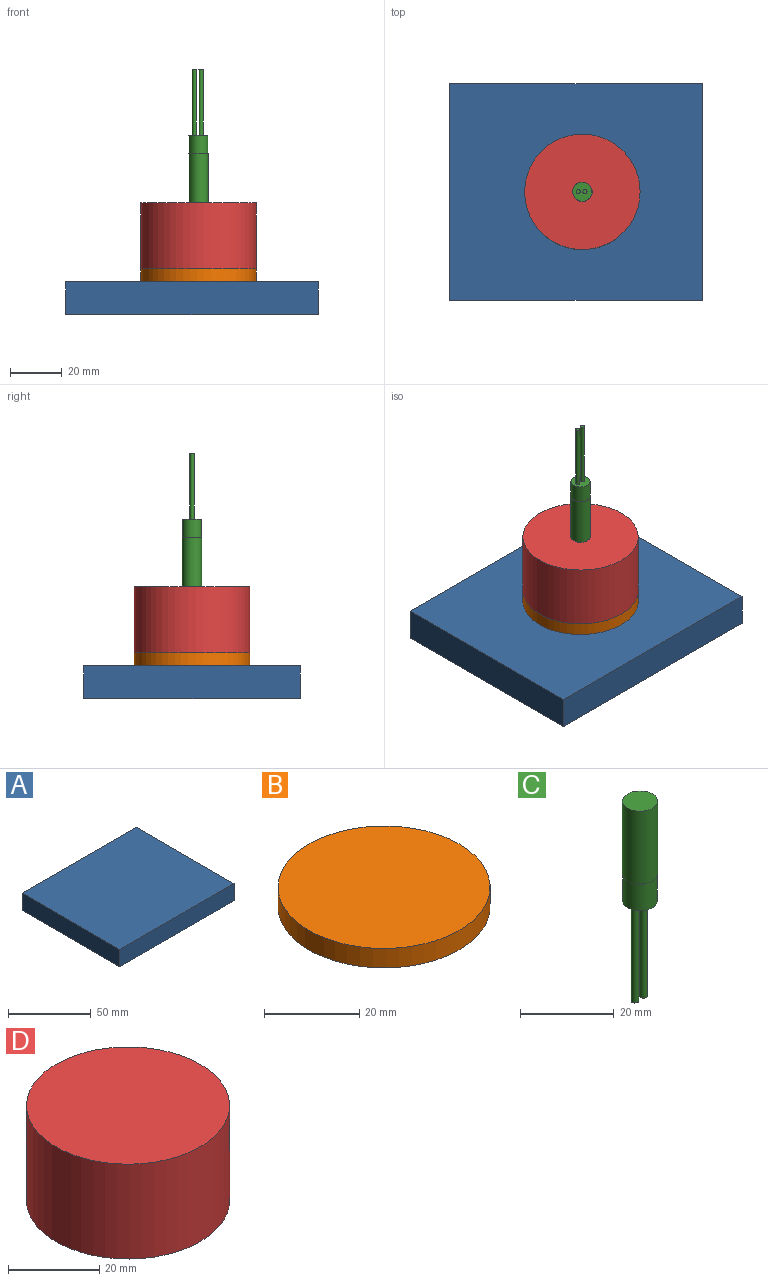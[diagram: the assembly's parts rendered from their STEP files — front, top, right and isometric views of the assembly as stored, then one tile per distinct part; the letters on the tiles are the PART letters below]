
ASSEMBLY  parts=4 mates=5
PART A: 6 faces, bbox 97.3x83.5x12.7 mm
  f0: plane 97.28x12.7mm, normal (0,1,0), area 1235.4mm2, adj f1,f3,f4,f5
  f1: plane 83.49x12.7mm, normal (-1,0,0), area 1060.3mm2, adj f0,f2,f4,f5
  f2: plane 97.28x12.7mm, normal (0,-1,0), area 1235.4mm2, adj f1,f3,f4,f5
  f3: plane 83.49x12.7mm, normal (1,0,0), area 1060.3mm2, adj f0,f2,f4,f5
  f4: plane 97.28x83.49mm, normal (0,0,1), area 8121.8mm2, adj f0,f1,f2,f3
  f5: plane 97.28x83.49mm, normal (0,0,-1), area 8121.8mm2, adj f0,f1,f2,f3
PART B: 3 faces, bbox 44.5x44.5x5 mm
  f0: cylinder r=22.23mm len=44.45mm, axis (0,0,-1), area 698.2mm2, adj f1,f2
  f1: plane 44.45x44.45mm, normal (0,0,1), area 1551.8mm2, adj f0
  f2: plane 44.45x44.45mm, normal (0,0,-1), area 1551.8mm2, adj f0
PART C: 9 faces, bbox 7.5x7.5x51.4 mm
  f0: cylinder r=3.68mm len=7.37mm, axis (0,0,1), area 161.6mm2, adj f1,f8
  f1: plane 7.37x7.37mm, normal (0,0,-1), area 38.7mm2, adj f0,f2,f4
  f2: cylinder r=0.79mm len=25.4mm, axis (0,0,1), area 125.7mm2, adj f1,f3
  f3: plane 1.57x1.57mm, normal (0,0,-1), area 1.9mm2, adj f2
  f4: cylinder r=0.79mm len=25.4mm, axis (0,0,1), area 125.7mm2, adj f1,f5
  f5: plane 1.57x1.57mm, normal (0,0,-1), area 1.9mm2, adj f4
  f6: cylinder r=3.75mm len=19.05mm, axis (0,0,-1), area 448.4mm2, adj f7,f8
  f7: plane 7.49x7.49mm, normal (0,0,1), area 44.1mm2, adj f6
  f8: plane 7.49x7.49mm, normal (0,0,-1), area 1.5mm2, adj f0,f6
PART D: 3 faces, bbox 44.5x44.5x25.4 mm
  f0: cylinder r=22.23mm len=44.45mm, axis (0,0,-1), area 3547mm2, adj f1,f2
  f1: plane 44.45x44.45mm, normal (0,0,1), area 1551.8mm2, adj f0
  f2: plane 44.45x44.45mm, normal (0,0,-1), area 1551.8mm2, adj f0
PLACE A t=(-27.26,3.06,-9.77)mm fixed
PLACE B t=(-22.84,-16.89,2.93)mm
PLACE C rot(axis=(1,0,0),180deg) t=(-22.84,-16.89,52.38)mm
PLACE D t=(-22.84,-16.89,7.93)mm
MATE planar B.f0 <-> D.f0  axis (0,0,1) through (-22.84,-16.89,7.93)mm
MATE cylindrical B.f0 <-> D.f0  axis (0,0,-1) through (-22.84,-16.89,5.43)mm
MATE planar B.f0 <-> A.f4  axis (0,0,-1) through (-22.84,-16.89,2.93)mm
MATE cylindrical C.f0 <-> D.f0  axis (0,0,1) through (-22.84,-16.89,42.85)mm
MATE planar C.f0 <-> D.f0  axis (0,0,-1) through (-22.84,-16.89,33.33)mm
